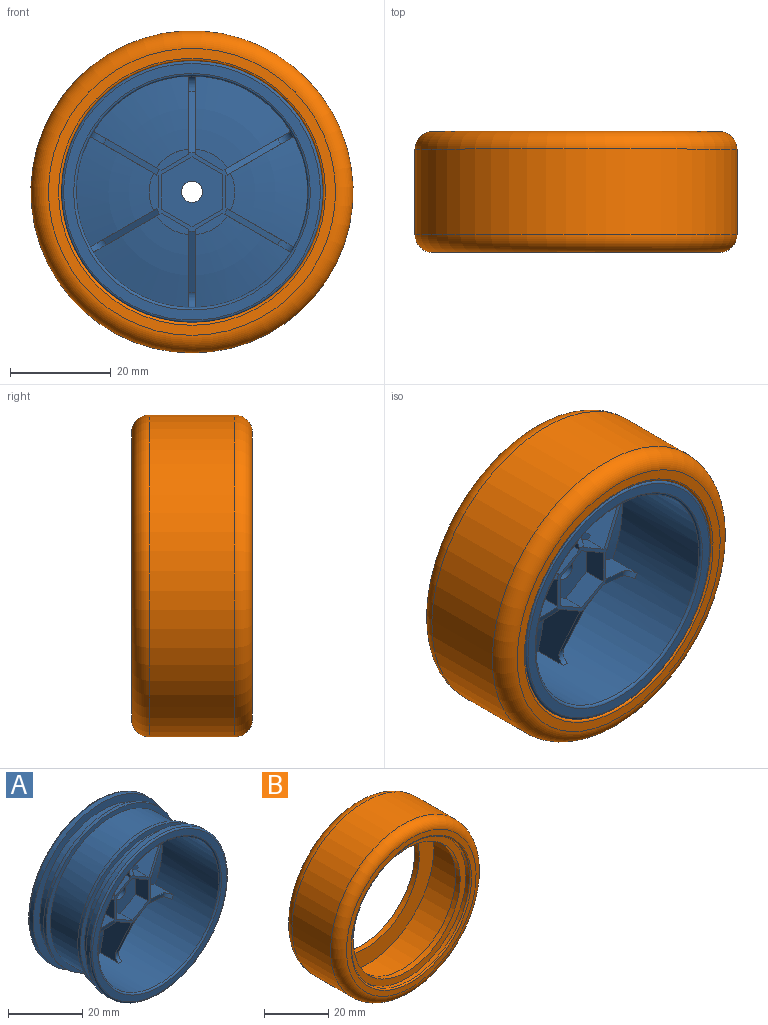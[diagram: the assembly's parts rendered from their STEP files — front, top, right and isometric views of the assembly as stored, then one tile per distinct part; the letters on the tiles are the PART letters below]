
ASSEMBLY  parts=2 mates=1
PART A: 82 faces, bbox 67.9x24.3x67.9 mm
  f0: cylinder r=8.5mm len=7.44mm, axis (0,1,0), area 38.9mm2, adj f2,f6,f68,f73
  f1: torus R=5.18mm, axis (0,1,0), area 221.4mm2, adj f4,f37,f53,f72
  f2: plane 7.44x1.75mm, normal (0,-1,0), area 10.5mm2, adj f0,f3,f68,f73
  f3: plane 6.41x4.6mm, normal (-1,0,0), area 29.5mm2, adj f2,f49,f68,f73
  f4: cylinder r=8.5mm len=6.44mm, axis (0,1,0), area 38.9mm2, adj f1,f39,f53,f72
  f5: cylinder r=8.5mm len=6.44mm, axis (0,1,0), area 38.9mm2, adj f7,f10,f64,f69
  f6: torus R=5.18mm, axis (0,1,0), area 221.4mm2, adj f0,f37,f68,f73
  f7: plane 6.44x4.24mm, normal (0,-1,0), area 10.5mm2, adj f5,f8,f64,f69
  f8: plane 5.55x4.6mm, normal (-0.5,0,-0.87), area 29.5mm2, adj f7,f49,f64,f69
  f9: cylinder r=8.5mm len=6.44mm, axis (0,1,0), area 38.9mm2, adj f11,f14,f60,f65
  f10: torus R=5.18mm, axis (0,1,0), area 221.4mm2, adj f5,f37,f64,f69
  f11: plane 6.44x4.24mm, normal (0,-1,0), area 10.5mm2, adj f9,f12,f60,f65
  f12: plane 5.55x4.6mm, normal (0.5,0,-0.87), area 29.5mm2, adj f11,f49,f60,f65
  f13: cylinder r=8.5mm len=7.44mm, axis (0,1,0), area 38.9mm2, adj f15,f18,f56,f61
  f14: torus R=5.18mm, axis (0,1,0), area 221.4mm2, adj f9,f37,f60,f65
  f15: plane 7.44x1.75mm, normal (0,-1,0), area 10.5mm2, adj f13,f16,f56,f61
  f16: plane 6.41x4.6mm, normal (1,0,0), area 29.5mm2, adj f15,f49,f56,f61
  f17: cylinder r=8.5mm len=6.44mm, axis (0,1,0), area 38.9mm2, adj f19,f38,f52,f57
  f18: torus R=5.18mm, axis (0,1,0), area 221.4mm2, adj f13,f37,f56,f61
  f19: plane 6.44x4.24mm, normal (0,-1,0), area 10.5mm2, adj f17,f20,f52,f57
  f20: plane 5.55x4.6mm, normal (0.5,0,0.87), area 29.5mm2, adj f19,f49,f52,f57
  f21: plane 5.55x4.6mm, normal (-0.5,0,0.87), area 29.5mm2, adj f39,f49,f53,f72
  f22: plane 51x51mm, normal (0,1,0), area 219mm2, adj f76,f79
  f23: cylinder r=26mm len=52mm, axis (0,1,0), area 245mm2, adj f24,f79
  f24: plane 52x52mm, normal (0,-1,0), area 388.7mm2, adj f23,f25
  f25: cylinder r=23.5mm len=47mm, axis (0,1,0), area 443mm2, adj f24,f26
  f26: plane 50.2x50.2mm, normal (0,1,0), area 244.3mm2, adj f25,f27
  f27: cylinder r=25.1mm len=50.2mm, axis (0,1,0), area 157.7mm2, adj f26,f28
  f28: plane 50.2x50.2mm, normal (0,-1,0), area 244.3mm2, adj f27,f29
  f29: cylinder r=23.5mm len=47mm, axis (0,1,0), area 1771.9mm2, adj f28,f30
  f30: plane 50.2x50.2mm, normal (0,1,0), area 244.3mm2, adj f29,f31
  f31: cylinder r=25.1mm len=50.2mm, axis (0,1,0), area 157.7mm2, adj f30,f32
  f32: plane 50.2x50.2mm, normal (0,-1,0), area 244.3mm2, adj f31,f33
  f33: cylinder r=23.5mm len=47mm, axis (0,1,0), area 443mm2, adj f32,f34
  f34: plane 52x52mm, normal (0,1,0), area 388.8mm2, adj f33,f35
  f35: cylinder r=26mm len=52mm, axis (0,1,0), area 245mm2, adj f34,f80
  f36: plane 51x51mm, normal (0,-1,0), area 307.9mm2, adj f80,f81
  f37: cylinder r=23mm len=46mm, axis (0,1,0), area 3056.7mm2, adj f1,f6,f10,f14,f18,f38,f51,f52
  f38: torus R=5.18mm, axis (0,1,0), area 221.4mm2, adj f17,f37,f52,f57
  f39: plane 6.44x4.24mm, normal (0,-1,0), area 10.5mm2, adj f4,f21,f53,f72
  f40: plane 11x11mm, normal (0,1,0), area 81.2mm2, adj f75,f78
  f41: cylinder r=6.5mm len=13mm, axis (0,1,0), area 84mm2, adj f77,f78
  f42: torus R=5.18mm, axis (0,1,0), area 1310.9mm2, adj f76,f77
  f43: plane 6x4.6mm, normal (0.5,0,0.87), area 31.9mm2, adj f44,f48,f49,f50
  f44: plane 6.93x4.6mm, normal (1,0,0), area 31.9mm2, adj f43,f45,f49,f50
  f45: plane 6x4.6mm, normal (0.5,0,-0.87), area 31.9mm2, adj f44,f46,f49,f50
  f46: plane 6x4.6mm, normal (-0.5,0,-0.87), area 31.9mm2, adj f45,f47,f49,f50
  f47: plane 6.93x4.6mm, normal (-1,0,0), area 31.9mm2, adj f46,f48,f49,f50
  f48: plane 6x4.6mm, normal (-0.5,0,0.87), area 31.9mm2, adj f43,f47,f49,f50
  f49: plane 15.59x14.1mm, normal (0,-1,0), area 34.4mm2, adj f3,f8,f12,f16,f20,f21,f43,f44
  f50: plane 13.86x12mm, normal (0,-1,0), area 110.9mm2, adj f43,f44,f45,f46,f47,f48,f75
  f51: cylinder r=2.31mm len=3mm, axis (-1,0,0), area 4.2mm2, adj f37,f52,f53,f54
  f52: plane 15.88x11.93mm, normal (1,0,0), area 104.9mm2, adj f17,f19,f20,f37,f38,f49,f51,f54
  f53: plane 15.88x11.93mm, normal (-1,0,0), area 104.9mm2, adj f1,f4,f21,f37,f39,f49,f51,f54
  f54: plane 12.21x5.6mm, normal (0,-0.91,0.42), area 16.1mm2, adj f49,f51,f52,f53
  f55: cylinder r=2.31mm len=3.19mm, axis (-0.5,0,0.87), area 4.2mm2, adj f37,f56,f57,f58
  f56: plane 13.8x11.93mm, normal (0.5,0,-0.87), area 105mm2, adj f13,f15,f16,f18,f37,f49,f55,f58
  f57: plane 13.8x11.93mm, normal (-0.5,0,0.87), area 105mm2, adj f17,f19,f20,f37,f38,f49,f55,f58
  f58: plane 11.17x7.14mm, normal (0.36,-0.91,0.21), area 16.1mm2, adj f49,f55,f56,f57
  f59: cylinder r=2.31mm len=3.19mm, axis (0.5,0,0.87), area 4.2mm2, adj f37,f60,f61,f62
  f60: plane 13.8x11.93mm, normal (-0.5,0,-0.87), area 105mm2, adj f9,f11,f12,f14,f37,f49,f59,f62
  f61: plane 13.8x11.93mm, normal (0.5,0,0.87), area 105mm2, adj f13,f15,f16,f18,f37,f49,f59,f62
  f62: plane 11.17x7.14mm, normal (0.36,-0.91,-0.21), area 16.1mm2, adj f49,f59,f60,f61
  f63: cylinder r=2.31mm len=2.99mm, axis (1,0,0), area 4.2mm2, adj f37,f64,f65,f66
  f64: plane 15.88x11.93mm, normal (-1,0,0), area 104.9mm2, adj f5,f7,f8,f10,f37,f49,f63,f66
  f65: plane 15.88x11.93mm, normal (1,0,0), area 105mm2, adj f9,f11,f12,f14,f37,f49,f63,f66
  f66: plane 12.21x5.6mm, normal (0,-0.91,-0.42), area 16.1mm2, adj f49,f63,f64,f65
  f67: cylinder r=2.31mm len=3.19mm, axis (0.5,0,-0.87), area 4.2mm2, adj f37,f68,f69,f70
  f68: plane 13.8x11.93mm, normal (-0.5,0,0.87), area 105mm2, adj f0,f2,f3,f6,f37,f49,f67,f70
  f69: plane 13.8x11.93mm, normal (0.5,0,-0.87), area 105mm2, adj f5,f7,f8,f10,f37,f49,f67,f70
  f70: plane 11.17x7.14mm, normal (-0.36,-0.91,-0.21), area 16.1mm2, adj f49,f67,f68,f69
  f71: cylinder r=2.31mm len=3.19mm, axis (-0.5,0,-0.87), area 4.2mm2, adj f37,f72,f73,f74
  f72: plane 13.8x11.93mm, normal (0.5,0,0.87), area 105mm2, adj f1,f4,f21,f37,f39,f49,f71,f74
  f73: plane 13.8x11.93mm, normal (-0.5,0,-0.87), area 105mm2, adj f0,f2,f3,f6,f37,f49,f71,f74
  f74: plane 11.17x7.14mm, normal (-0.36,-0.91,0.21), area 16.1mm2, adj f49,f71,f72,f73
  f75: cylinder r=2.1mm len=4.2mm, axis (0,-1,0), area 26.4mm2, adj f40,f50
  f76: torus R=24.09mm, axis (0,-1,0), area 306.6mm2, adj f22,f42
  f77: torus R=8.5mm, axis (0,-1,0), area 138.3mm2, adj f41,f42
  f78: torus R=5.5mm, axis (0,-1,0), area 60.6mm2, adj f40,f41
  f79: torus R=25.5mm, axis (0,-1,0), area 127.4mm2, adj f22,f23
  f80: torus R=25.5mm, axis (0,1,0), area 127.4mm2, adj f35,f36
  f81: torus R=23.5mm, axis (0,1,0), area 114.4mm2, adj f36,f37
PART B: 16 faces, bbox 69.3x24x69.3 mm
  f0: torus R=28.5mm, axis (0,-1,0), area 1061.5mm2, adj f1,f15
  f1: cylinder r=32mm len=64mm, axis (0,-1,0), area 3418.1mm2, adj f0,f2
  f2: torus R=28.5mm, axis (0,-1,0), area 1061.5mm2, adj f1,f3
  f3: plane 57x57mm, normal (0,-1,0), area 345.6mm2, adj f2,f4
  f4: torus R=26.5mm, axis (0,-1,0), area 129.2mm2, adj f3,f5
  f5: cylinder r=26mm len=52mm, axis (0,-1,0), area 245mm2, adj f4,f6
  f6: plane 52x52mm, normal (0,-1,0), area 388.8mm2, adj f5,f7
  f7: cylinder r=23.5mm len=47mm, axis (0,-1,0), area 295.3mm2, adj f6,f8
  f8: plane 60x60mm, normal (0,1,0), area 1092.5mm2, adj f7,f9
  f9: cylinder r=30mm len=60mm, axis (0,-1,0), area 3015.9mm2, adj f8,f10
  f10: plane 60x60mm, normal (0,-1,0), area 1092.5mm2, adj f9,f11
  f11: cylinder r=23.5mm len=47mm, axis (0,-1,0), area 295.3mm2, adj f10,f12
  f12: plane 52x52mm, normal (0,1,0), area 388.8mm2, adj f11,f13
  f13: cylinder r=26mm len=52mm, axis (0,-1,0), area 245mm2, adj f12,f14
  f14: torus R=26.5mm, axis (0,-1,0), area 129.2mm2, adj f13,f15
  f15: plane 57x57mm, normal (0,1,0), area 345.6mm2, adj f0,f14
PLACE A at identity fixed
PLACE B at identity
MATE fastened B.f0 <-> A.f0  axis (0,-1,0) through (0,-10,0)mm
